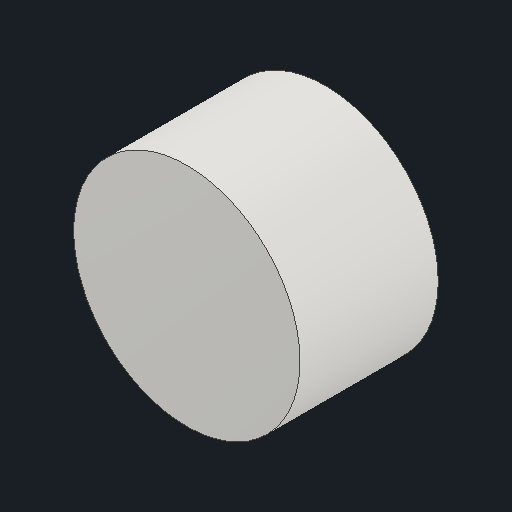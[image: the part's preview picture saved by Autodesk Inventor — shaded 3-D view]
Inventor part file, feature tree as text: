
AUTODESK INVENTOR PART (.ipt)
format: ipt  version: 2023.1 (Build 271208000, 208)  size: 84,480 bytes
history: native  units: mm (DEFAULTED — no unit token found)
features: extrude x1, other x1
ambient origin geometry x8: Origin, YZ Plane, XZ Plane, XY Plane, X Axis, Y Axis, Z Axis, Center Point
bodies: Solid1 (feature_tree)
feature tree (2):
  extrude  "Pulley"  Depth=18.0mm
  other  "Main Sketch"
